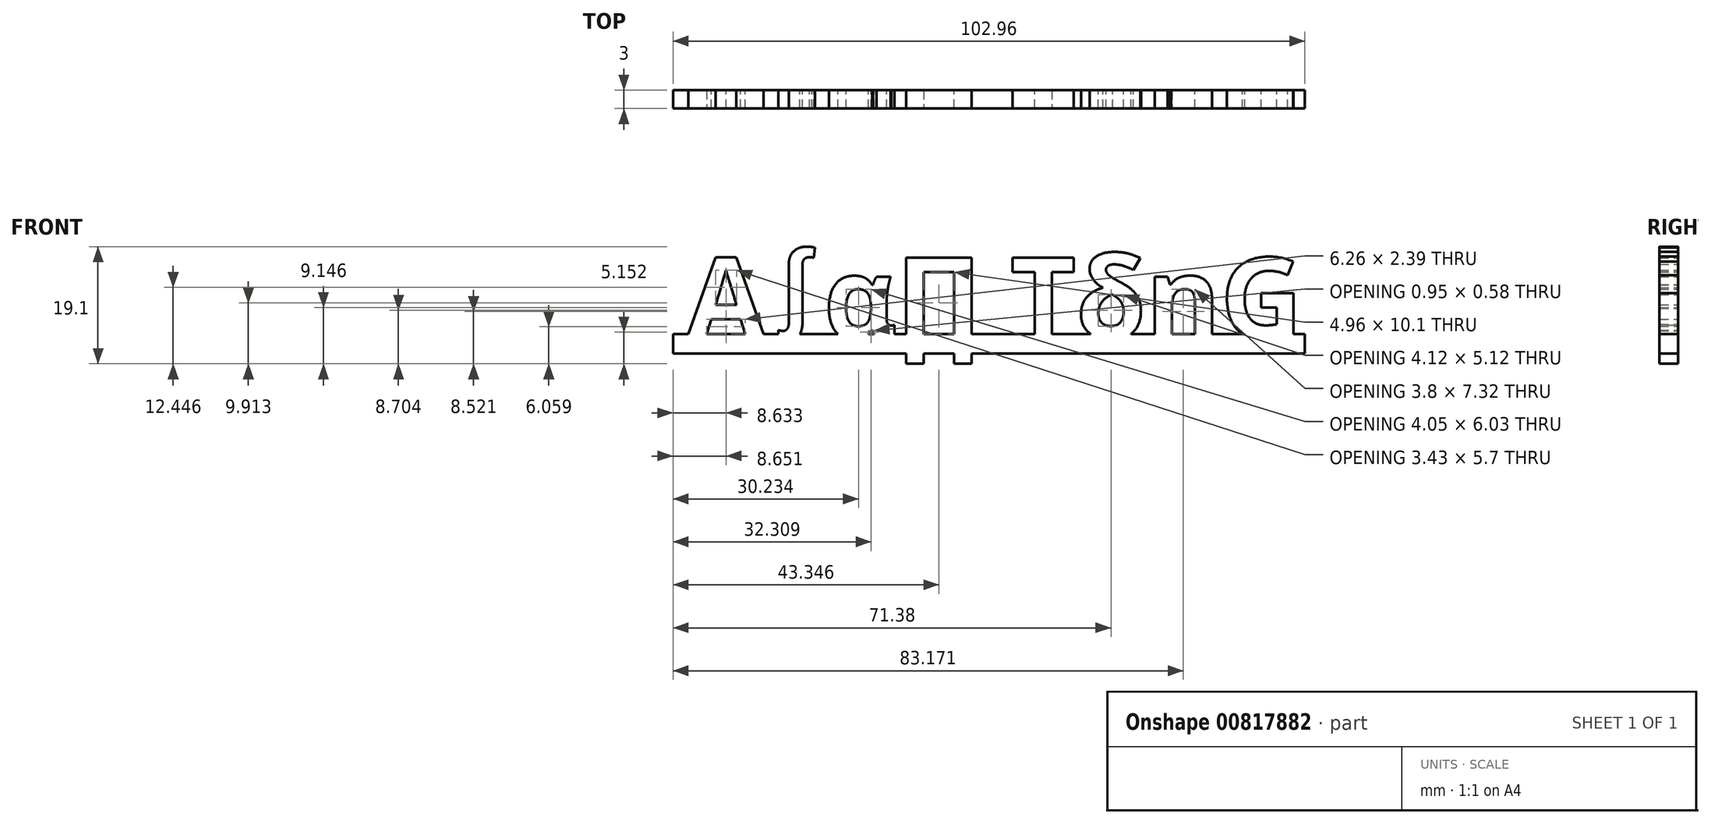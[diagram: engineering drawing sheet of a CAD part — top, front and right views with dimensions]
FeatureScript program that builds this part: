
annotation { "Feature Type Name" : "Feature", "Feature Type Description" : "" }
export const myFeature = defineFeature(function(context is Context, id is Id, definition is map)
    precondition{}
    {
        {
            var Q0;
            Q0=qCreatedBy(makeId("Front.planeOp"),FACE);
            var sketch = newSketch(context, id + "F0", { "sketchPlane" : qUnion([Q0])});
            skText(sketch, "E0", { "text": "A  α∏ TδnG \n\n", "fontName": "OpenSans-Bold.ttf"});
            skText(sketch, "E1", { "text": "∫", "fontName": "RobotoSlab-Bold.ttf"});
            const initialGuessF0  = {"E0": [-0.05, 0, 1, 0, 0.01328], "E1": [-0.03446, 0.00287, 1, 0, 0.01129]};
            skSetInitialGuess(sketch, initialGuessF0);
            skSolve(sketch);
        }
        {
            var Q0;
            Q0 = qSketchRegion(id + "F0", true);
            extrude(context, id + "F1", {"entities" : qUnion([Q0]), "depth" : 3 * mm, "offsetDistance" : 25.4 * mm});
        }
        {
            var Q0;
            Q0=qCreatedBy(makeId("Front.planeOp"),FACE);
            var sketch = newSketch(context, id + "F2", { "sketchPlane" : qUnion([Q0])});
            skLineSegment(sketch, "E2.bottom", {"start": v(-52.27, 0.74) * mm, "end": v(50.7, 0.74) * mm});
            skLineSegment(sketch, "E2.top", {"start": v(-52.27, -2.42) * mm, "end": v(50.7, -2.42) * mm});
            skLineSegment(sketch, "E2.left", {"start": v(-52.27, 0.74) * mm, "end": v(-52.27, -2.42) * mm});
            skLineSegment(sketch, "E2.right", {"start": v(50.7, 0.74) * mm, "end": v(50.7, -2.42) * mm});
            skSolve(sketch);
        }
        {
            var Q0;
            Q0 = qSketchRegion(id + "F2", true);
            extrude(context, id + "F3", {"entities" : qUnion([Q0]), "operationType" : NewBodyOperationType.ADD, "depth" : 3 * mm, "offsetDistance" : 25.4 * mm});
        }
    });
